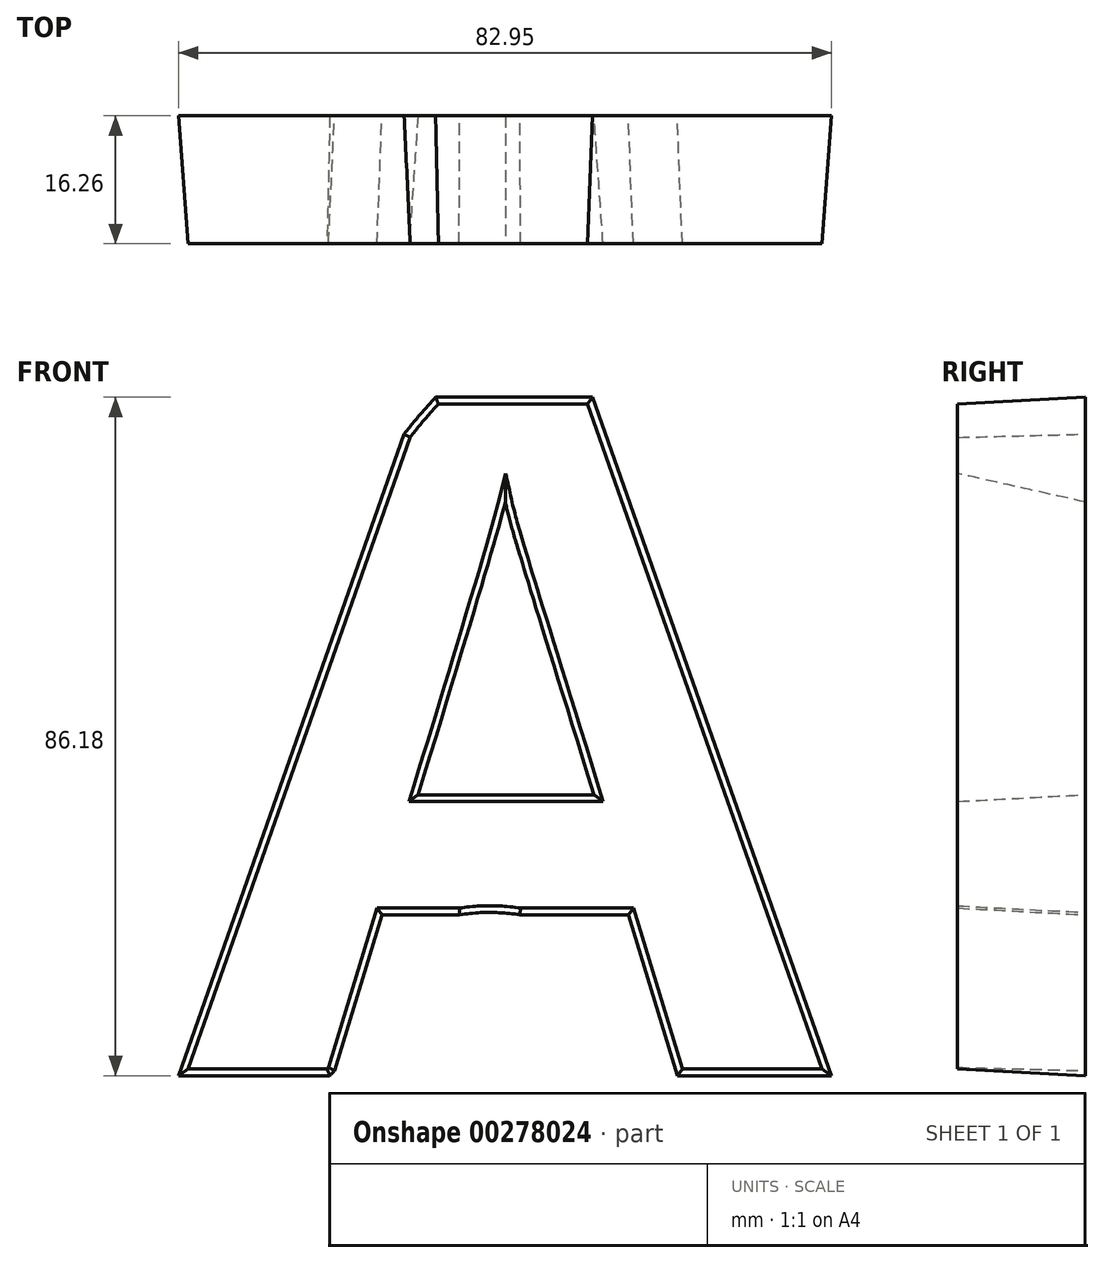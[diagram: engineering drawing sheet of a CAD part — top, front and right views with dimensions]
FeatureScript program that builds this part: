
annotation { "Feature Type Name" : "Feature", "Feature Type Description" : "" }
export const myFeature = defineFeature(function(context is Context, id is Id, definition is map)
    precondition{}
    {
        {
            var Q0;
            Q0=qCreatedBy(makeId("Front.planeOp"),FACE);
            var sketch = newSketch(context, id + "F0", { "sketchPlane" : qUnion([Q0])});
            skLineSegment(sketch, "E0.bottom", {"start": v(-56.08, 58.98) * mm, "end": v(59.13, 58.98) * mm});
            skLineSegment(sketch, "E0.top", {"start": v(-56.08, -58.06) * mm, "end": v(59.13, -58.06) * mm});
            skLineSegment(sketch, "E0.left", {"start": v(-56.08, 58.98) * mm, "end": v(-56.08, -58.06) * mm});
            skLineSegment(sketch, "E0.right", {"start": v(59.13, 58.98) * mm, "end": v(59.13, -58.06) * mm});
            skText(sketch, "E1", { "text": "A", "fontName": "OpenSans-Bold.ttf"});
            skFitSpline(sketch, "E2", {"points": [v(3.35, 41.3) * mm, v(-27.43, -42.82) * mm, v(-8.23, -42.82) * mm, v(2.44, -24.54) * mm, v(25.6, -26.67) * mm, v(31.09, -42.82) * mm, v(59.13, -46.48) * mm, v(27.74, 43.74) * mm, v(3.35, 41.3) * mm]});
            const initialGuessF0  = {"E1": [-0.02743, -0.04282, 1, 0, 0.08656]};
            skSetInitialGuess(sketch, initialGuessF0);
            skSolve(sketch);
        }
        {
            var Q0;
            {var subQ12=sQuery(id+"F0.wireOp",EDGE,"E1.sketch_text.stroke-0");Q0=makeQuery(id+"F0.imprint","IMPRINT",FACE,{"disambiguationData":[TD([[makeQuery(id+"F0.imprint","IMPRINT",EDGE,{"derivedFrom":subQ12}),-1.0]])]});}
            extrude(context, id + "F1", {"entities" : qUnion([Q0]), "depth" : 16.26 * mm, "hasDraft" : true, "draftAngle" : 3 * degree, "draftPullDirection" : true});
        }
    });
